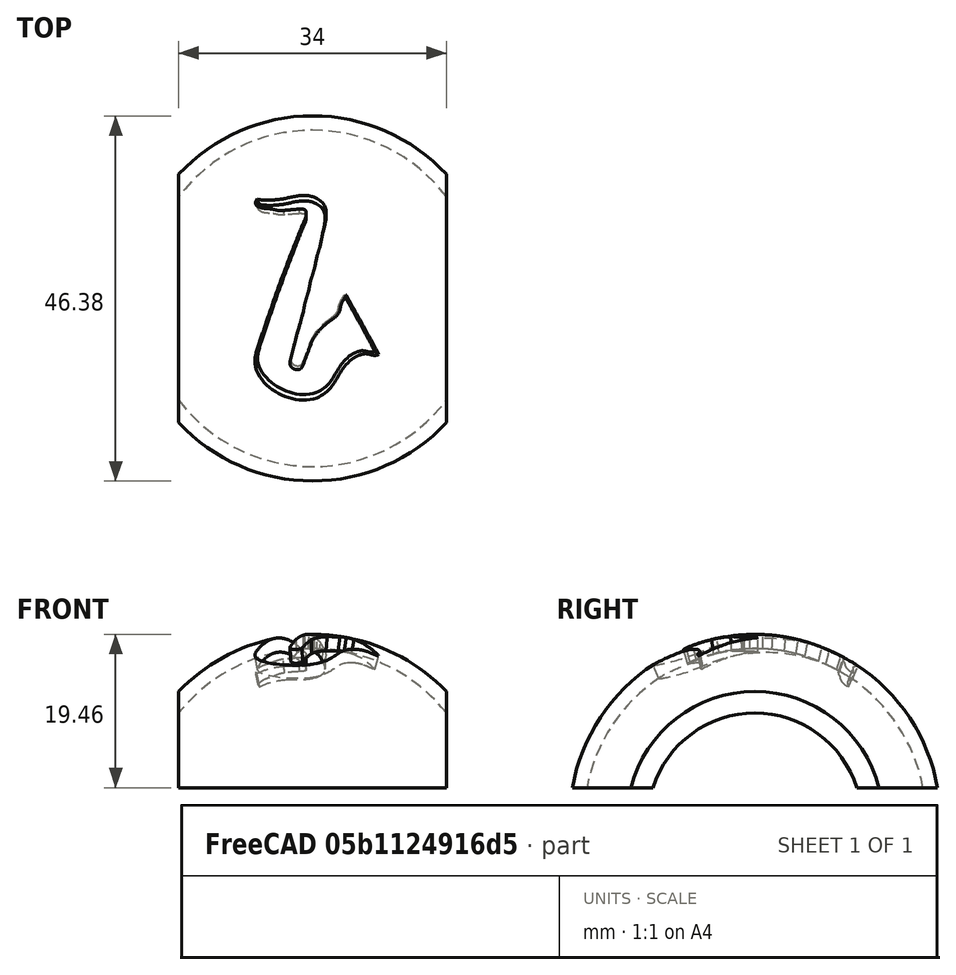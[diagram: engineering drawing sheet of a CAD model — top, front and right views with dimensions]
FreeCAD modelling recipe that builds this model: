
FCSTD DOCUMENT  (FreeCAD 0.19R24276 (Git))
Label: ballmarker
License: All rights reserved
LicenseURL: http://en.wikipedia.org/wiki/All_rights_reserved
objects: Part::Sphere×2, Part::Box×2, Part::Feature×1, Part::FeaturePython×1, Part::Loft×1, Part::MultiFuse×1, Part::Cut×1
note: 9 computed .brp shape members not serialized (recipe doc carries the construction recipe); baked Part::Feature solids carry a one-line shape summary decoded from their .brp

FEATURE [Part::Sphere] Sphere
  Angle1 = 10
  Angle2 = 90
  Angle3 = 360
  AttacherType = Attacher::AttachEngine3D
  Radius = 23.55
FEATURE [Part::Sphere] Sphere001
  Angle1 = -90
  Angle2 = 90
  Angle3 = 360
  AttacherType = Attacher::AttachEngine3D
  Radius = 21.75
FEATURE [Part::Box] Box  label="Cube"
  AttacherType = Attacher::AttachEngine3D
  Height = 40
  Length = 15
  Placement = pos=(17,-20,0) rot=(0,0,1;0rad)
  Width = 40
  expr: .Placement.Base.y = -20
  expr: .Placement.Base.x = 17
FEATURE [Part::Box] Box001  label="Cube001"
  AttacherType = Attacher::AttachEngine3D
  Height = 40
  Length = 15
  Placement = pos=(-32,-20,0) rot=(0,0,1;0rad)
  Width = 40
FEATURE [Part::Feature] Selection001  label="Selection002"
  Placement = pos=(-3.72,16.08,11) rot=(0,0,-1;0.547161rad)
  shape: bbox 23.77 x 24.01 x 2e-07 mm, 1 faces, 0 solids (baked)
FEATURE [Part::FeaturePython] Clone001  label="Selection003"  # Draft clone (typed FeaturePython)
  AttacherType = Attacher::AttachEngine3D
  Fuse = false
  Objects = -> [Selection001]
  Placement = pos=(-5.72,27.08,27) rot=(0,0,-1;0.547161rad)
  Scale = (1.7,1.7,1.7)
FEATURE [Part::Loft] Loft001
  Closed = false
  MaxDegree = 5
  Ruled = false
  Sections = -> [Selection001,Clone001]
  Solid = true
FEATURE [Part::MultiFuse] Fusion
  Shapes = -> [Box,Sphere001,Box001,Loft001]
FEATURE [Part::Cut] Cut
  Base = -> Sphere
  Tool = -> Fusion
